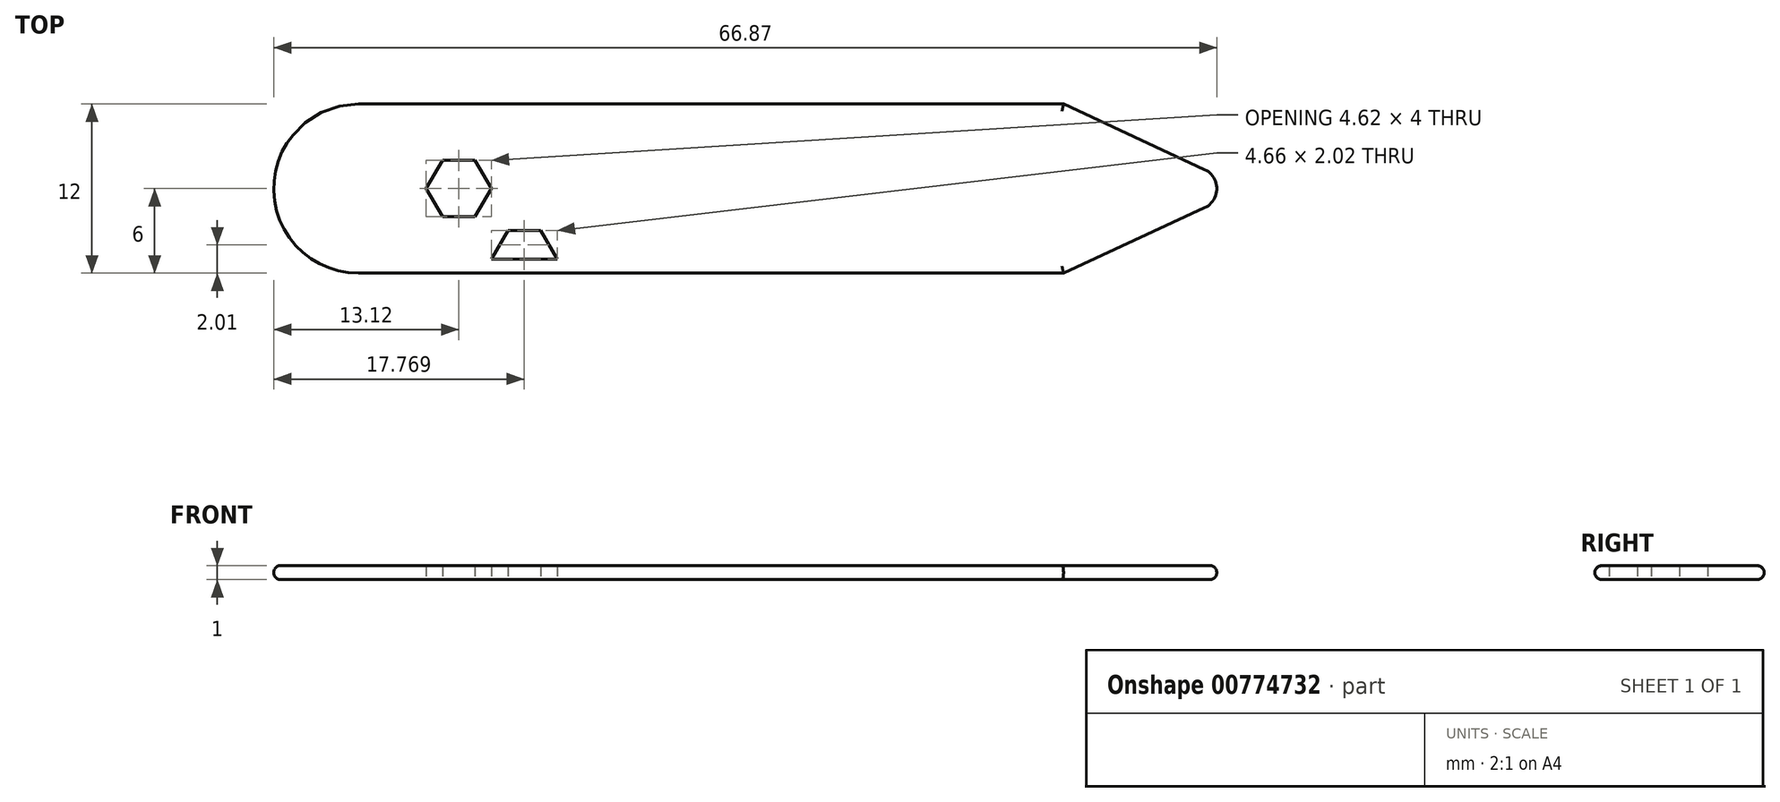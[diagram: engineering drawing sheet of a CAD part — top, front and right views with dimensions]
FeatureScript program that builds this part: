
annotation { "Feature Type Name" : "Feature", "Feature Type Description" : "" }
export const myFeature = defineFeature(function(context is Context, id is Id, definition is map)
    precondition{}
    {
        {
            var Q0;
            Q0=qCreatedBy(makeId("Top.planeOp"),FACE);
            var sketch = newSketch(context, id + "F0", { "sketchPlane" : qUnion([Q0])});
            skLineSegment(sketch, "E0.bottom", {"start": v(-25, 6) * mm, "end": v(25, 6) * mm});
            skLineSegment(sketch, "E0.top", {"start": v(-25, -6) * mm, "end": v(25, -6) * mm});
            skPoint(sketch, "E0.middle", {"position": v(0, 0) * mm});
            skLineSegment(sketch, "E1", {"start": v(25, 6) * mm, "end": v(35, 1.36) * mm});
            skLineSegment(sketch, "E2", {"start": v(35, -1.36) * mm, "end": v(25, -6) * mm});
            skPoint(sketch, "E3.visualSharp", {"position": v(37.93, 0) * mm});
            skArc(sketch, "E3.filletArc", {"start": v(35, -1.36) * mm, "mid": v(35.87, 0) * mm, "end": v(35, 1.36) * mm});
            skArc(sketch, "E4", {"start": v(-25, 6) * mm, "mid": v(-31, 0) * mm, "end": v(-25, -6) * mm});
            skLineSegment(sketch, "E5", {"start": v(-31, 0) * mm, "end": v(35.87, 0) * mm, "construction": true});
            skCircle(sketch, "E6.cCircle", {"center": v(-17.88, 0) * mm, "radius": 2 * mm, "construction": true});
            skLineSegment(sketch, "E6.0", {"start": v(-20.19, 0) * mm, "end": v(-19.03, 2) * mm});
            skLineSegment(sketch, "E6.1", {"start": v(-19.03, 2) * mm, "end": v(-16.72, 2) * mm});
            skLineSegment(sketch, "E6.2", {"start": v(-16.72, 2) * mm, "end": v(-15.57, 0) * mm});
            skLineSegment(sketch, "E6.3", {"start": v(-15.57, 0) * mm, "end": v(-16.72, -2) * mm});
            skLineSegment(sketch, "E6.4", {"start": v(-16.72, -2) * mm, "end": v(-19.03, -2) * mm});
            skLineSegment(sketch, "E6.5", {"start": v(-19.03, -2) * mm, "end": v(-20.19, 0) * mm});
            skPoint(sketch, "E6.0.midPoint", {"position": v(-19.61, 1) * mm});
            skLineSegment(sketch, "E7.0", {"start": v(-25, -5) * mm, "end": v(25, -5) * mm, "construction": true});
            skLineSegment(sketch, "E8.0", {"start": v(-25, 5) * mm, "end": v(25, 5) * mm, "construction": true});
            skLineSegment(sketch, "E9.0", {"start": v(-15.56, -5) * mm, "end": v(-14.4, -2.98) * mm});
            skLineSegment(sketch, "E9.1", {"start": v(-14.4, -2.98) * mm, "end": v(-12.07, -2.98) * mm});
            skLineSegment(sketch, "E9.2", {"start": v(-12.07, -2.98) * mm, "end": v(-10.9, -5) * mm});
            skLineSegment(sketch, "E10", {"start": v(-15.56, -5) * mm, "end": v(-10.9, -5) * mm});
            skSolve(sketch);
        }
        {
            var Q0;
            Q0=makeQuery(id+"F0.imprint","IMPRINT",FACE,{"disambiguationData":[TD([[makeQuery(id+"F0.imprint","IMPRINT",EDGE,{"derivedFrom":sQuery(id+"F0.wireOp",EDGE,"E0.bottom")}),-1.0]])]});
            extrude(context, id + "F1", {"entities" : qUnion([Q0]), "depth" : 1 * mm, "offsetDistance" : 25 * mm});
        }
        {
            var Q0;
            Q0=makeQuery(id+"F1.opExtrude","CAP_EDGE",EDGE,{"disambiguationData":[OSD([sQuery(id+"F0.wireOp",EDGE,"E0.top")])],"isStart":false});
            var Q1;
            Q1=makeQuery(id+"F1.opExtrude","CAP_EDGE",EDGE,{"disambiguationData":[OSD([sQuery(id+"F0.wireOp",EDGE,"E4")])],"isStart":false});
            var Q2;
            Q2=makeQuery(id+"F1.opExtrude","CAP_EDGE",EDGE,{"disambiguationData":[OSD([sQuery(id+"F0.wireOp",EDGE,"E0.bottom")])],"isStart":false});
            var Q3;
            Q3=makeQuery(id+"F1.opExtrude","CAP_EDGE",EDGE,{"disambiguationData":[OSD([sQuery(id+"F0.wireOp",EDGE,"E2")])],"isStart":false});
            var Q4;
            Q4=makeQuery(id+"F1.opExtrude","CAP_EDGE",EDGE,{"disambiguationData":[OSD([sQuery(id+"F0.wireOp",EDGE,"E3.filletArc")])],"isStart":false});
            var Q5;
            Q5=makeQuery(id+"F1.opExtrude","CAP_EDGE",EDGE,{"disambiguationData":[OSD([sQuery(id+"F0.wireOp",EDGE,"E1")])],"isStart":false});
            var Q6;
            Q6=makeQuery(id+"F1.opExtrude","CAP_EDGE",EDGE,{"disambiguationData":[OSD([sQuery(id+"F0.wireOp",EDGE,"E0.top")])],"isStart":true});
            var Q7;
            Q7=makeQuery(id+"F1.opExtrude","CAP_EDGE",EDGE,{"disambiguationData":[OSD([sQuery(id+"F0.wireOp",EDGE,"E2")])],"isStart":true});
            var Q8;
            Q8=makeQuery(id+"F1.opExtrude","CAP_EDGE",EDGE,{"disambiguationData":[OSD([sQuery(id+"F0.wireOp",EDGE,"E4")])],"isStart":true});
            var Q9;
            Q9=makeQuery(id+"F1.opExtrude","CAP_EDGE",EDGE,{"disambiguationData":[OSD([sQuery(id+"F0.wireOp",EDGE,"E0.bottom")])],"isStart":true});
            var Q10;
            Q10=makeQuery(id+"F1.opExtrude","CAP_EDGE",EDGE,{"disambiguationData":[OSD([sQuery(id+"F0.wireOp",EDGE,"E1")])],"isStart":true});
            var Q11;
            Q11=makeQuery(id+"F1.opExtrude","CAP_EDGE",EDGE,{"disambiguationData":[OSD([sQuery(id+"F0.wireOp",EDGE,"E3.filletArc")])],"isStart":true});
            fillet(context, id + "F2", {"entities" : qUnion([Q0, Q1, Q2, Q3, Q4, Q5, Q6, Q7, Q8, Q9, Q10, Q11]), "radius" : 0.5 * mm, "tangentPropagation" : true, "allowEdgeOverflow" : false});
        }
    });
